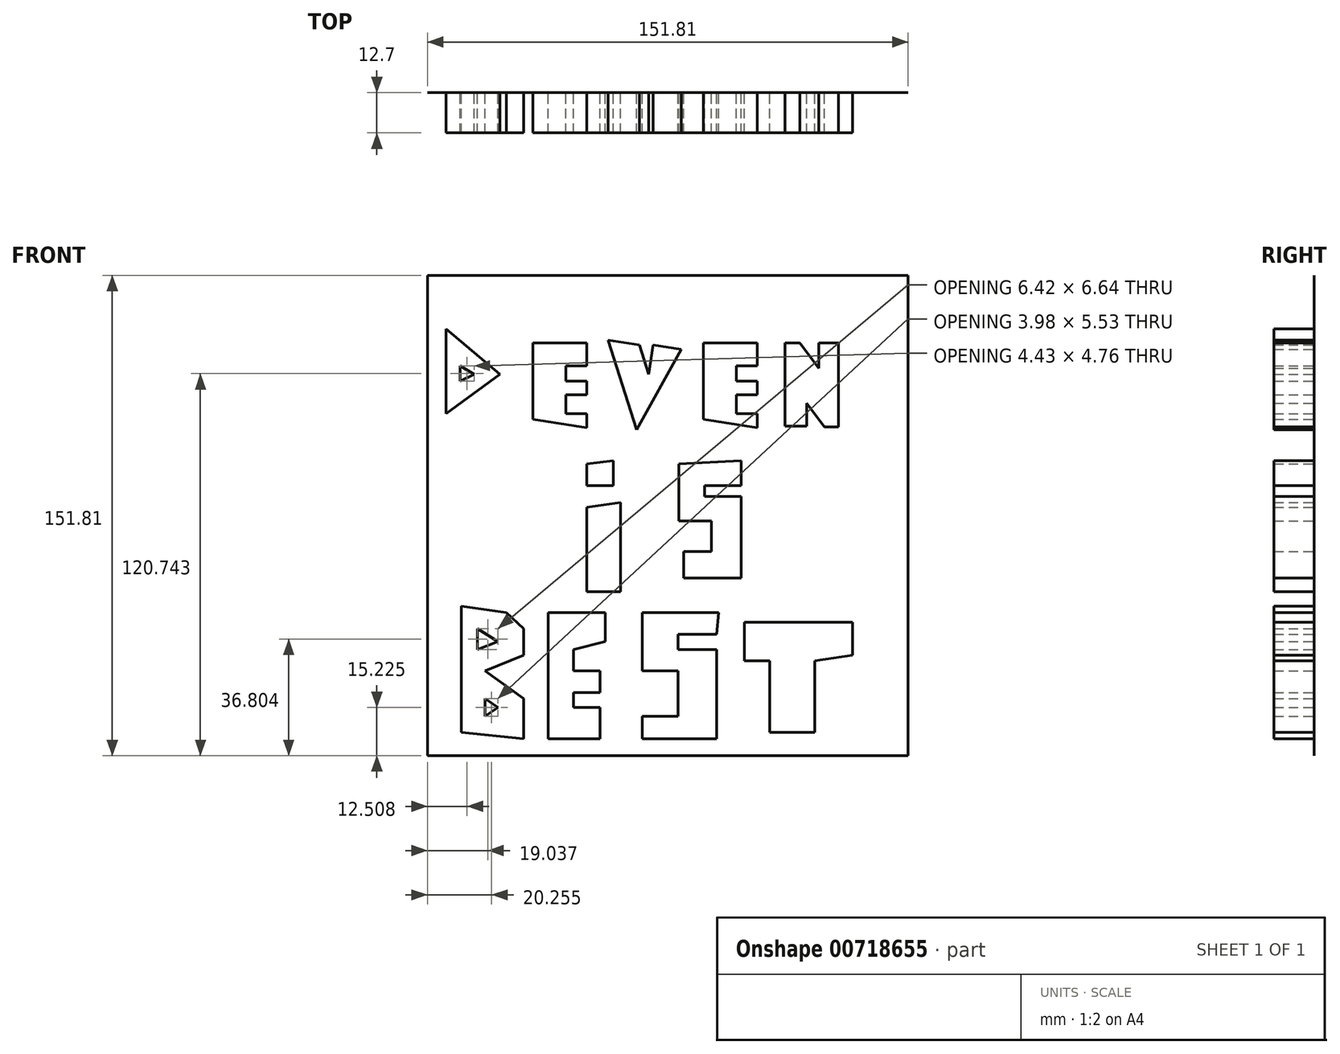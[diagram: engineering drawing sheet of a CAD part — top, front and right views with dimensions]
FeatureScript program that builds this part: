
annotation { "Feature Type Name" : "Feature", "Feature Type Description" : "" }
export const myFeature = defineFeature(function(context is Context, id is Id, definition is map)
    precondition{}
    {
        {
            var Q0;
            Q0=qCreatedBy(makeId("Front.planeOp"),FACE);
            var sketch = newSketch(context, id + "F0", { "sketchPlane" : qUnion([Q0])});
            skLineSegment(sketch, "E0", {"start": v(-70.27, 58.87) * mm, "end": v(-70.27, 32.1) * mm});
            skLineSegment(sketch, "E1", {"start": v(-70.27, 58.87) * mm, "end": v(-53.23, 44.49) * mm});
            skLineSegment(sketch, "E2", {"start": v(-70.27, 32.1) * mm, "end": v(-53.23, 44.49) * mm});
            skLineSegment(sketch, "E3", {"start": v(-42.83, 54.45) * mm, "end": v(-42.83, 30.32) * mm});
            skLineSegment(sketch, "E4", {"start": v(-65.85, 47.14) * mm, "end": v(-65.85, 42.38) * mm});
            skPoint(sketch, "E4.endSnap0", {"position": v(-42.83, 42.38) * mm});
            skLineSegment(sketch, "E5", {"start": v(-65.85, 42.38) * mm, "end": v(-61.42, 44.49) * mm});
            skLineSegment(sketch, "E6", {"start": v(-65.85, 47.14) * mm, "end": v(-61.42, 44.49) * mm});
            skLineSegment(sketch, "E7", {"start": v(-42.83, 54.45) * mm, "end": v(-25.78, 54.45) * mm});
            skLineSegment(sketch, "E8", {"start": v(-25.78, 52.68) * mm, "end": v(-25.78, 47.14) * mm});
            skLineSegment(sketch, "E9", {"start": v(-25.78, 47.14) * mm, "end": v(-32.42, 47.14) * mm});
            skLineSegment(sketch, "E10", {"start": v(-25.78, 54.45) * mm, "end": v(-25.78, 47.14) * mm});
            skLineSegment(sketch, "E11", {"start": v(-32.42, 47.14) * mm, "end": v(-32.42, 42.38) * mm});
            skLineSegment(sketch, "E12", {"start": v(-32.42, 42.38) * mm, "end": v(-25.78, 42.38) * mm});
            skLineSegment(sketch, "E13", {"start": v(-25.78, 42.38) * mm, "end": v(-25.78, 38.07) * mm});
            skLineSegment(sketch, "E14", {"start": v(-25.78, 38.07) * mm, "end": v(-32.42, 38.07) * mm});
            skLineSegment(sketch, "E15", {"start": v(-32.42, 38.07) * mm, "end": v(-32.42, 32.1) * mm});
            skLineSegment(sketch, "E16", {"start": v(-32.42, 32.1) * mm, "end": v(-25.78, 32.1) * mm});
            skLineSegment(sketch, "E17", {"start": v(-25.78, 32.1) * mm, "end": v(-25.78, 27.67) * mm});
            skLineSegment(sketch, "E18", {"start": v(-25.78, 27.67) * mm, "end": v(-42.83, 30.32) * mm});
            skLineSegment(sketch, "E19", {"start": v(-19.14, 55.33) * mm, "end": v(-10.07, 27) * mm});
            skLineSegment(sketch, "E20", {"start": v(-10.07, 27) * mm, "end": v(4.1, 52.45) * mm});
            skLineSegment(sketch, "E21", {"start": v(4.1, 52.45) * mm, "end": v(-4.8, 53.84) * mm});
            skLineSegment(sketch, "E22", {"start": v(-4.8, 53.84) * mm, "end": v(-6.24, 44.56) * mm});
            skLineSegment(sketch, "E23", {"start": v(-6.24, 44.56) * mm, "end": v(-9.22, 53.84) * mm});
            skLineSegment(sketch, "E24", {"start": v(-9.22, 53.84) * mm, "end": v(-19.14, 55.33) * mm});
            skLineSegment(sketch, "E25", {"start": v(10.97, 54.45) * mm, "end": v(10.97, 30.32) * mm});
            skPoint(sketch, "E26.endSnap0", {"position": v(10.97, 42.38) * mm});
            skLineSegment(sketch, "E27", {"start": v(10.97, 54.45) * mm, "end": v(28.01, 54.45) * mm});
            skLineSegment(sketch, "E28", {"start": v(28.01, 52.68) * mm, "end": v(28.01, 47.14) * mm});
            skLineSegment(sketch, "E29", {"start": v(28.01, 47.14) * mm, "end": v(21.37, 47.14) * mm});
            skLineSegment(sketch, "E30", {"start": v(28.01, 54.45) * mm, "end": v(28.01, 47.14) * mm});
            skLineSegment(sketch, "E31", {"start": v(21.37, 47.14) * mm, "end": v(21.37, 42.38) * mm});
            skLineSegment(sketch, "E32", {"start": v(21.37, 42.38) * mm, "end": v(28.01, 42.38) * mm});
            skLineSegment(sketch, "E33", {"start": v(28.01, 42.38) * mm, "end": v(28.01, 38.07) * mm});
            skLineSegment(sketch, "E34", {"start": v(28.01, 38.07) * mm, "end": v(21.37, 38.07) * mm});
            skLineSegment(sketch, "E35", {"start": v(21.37, 38.07) * mm, "end": v(21.37, 32.1) * mm});
            skLineSegment(sketch, "E36", {"start": v(21.37, 32.1) * mm, "end": v(28.01, 32.1) * mm});
            skLineSegment(sketch, "E37", {"start": v(28.01, 32.1) * mm, "end": v(28.01, 27.67) * mm});
            skLineSegment(sketch, "E38", {"start": v(28.01, 27.67) * mm, "end": v(10.97, 30.32) * mm});
            skLineSegment(sketch, "E39", {"start": v(36.85, 54.45) * mm, "end": v(36.85, 28.1) * mm});
            skLineSegment(sketch, "E40", {"start": v(36.85, 28.1) * mm, "end": v(43.71, 28.1) * mm});
            skLineSegment(sketch, "E41", {"start": v(43.71, 28.1) * mm, "end": v(43.71, 35.41) * mm});
            skLineSegment(sketch, "E42", {"start": v(49.25, 27.89) * mm, "end": v(53.67, 27.89) * mm});
            skLineSegment(sketch, "E43", {"start": v(53.67, 27.89) * mm, "end": v(53.67, 54.45) * mm});
            skLineSegment(sketch, "E44", {"start": v(53.67, 54.45) * mm, "end": v(47.47, 54.45) * mm});
            skLineSegment(sketch, "E45", {"start": v(47.47, 56.66) * mm, "end": v(47.47, 46.48) * mm});
            skLineSegment(sketch, "E46", {"start": v(47.47, 46.48) * mm, "end": v(41.5, 54.45) * mm});
            skLineSegment(sketch, "E47", {"start": v(41.5, 54.45) * mm, "end": v(36.85, 54.45) * mm});
            skLineSegment(sketch, "E48", {"start": v(43.71, 35.41) * mm, "end": v(49.25, 27.89) * mm});
            skSolve(sketch);
        }
        {
            var Q0;
            Q0 = qSketchRegion(id + "F0", true);
            extrude(context, id + "F1", {"entities" : qUnion([Q0]), "depth" : 12.7 * mm, "offsetDistance" : 25.4 * mm});
        }
        {
            var Q0;
            Q0=qCreatedBy(makeId("Front.planeOp"),FACE);
            var sketch = newSketch(context, id + "F2", { "sketchPlane" : qUnion([Q0])});
            skLineSegment(sketch, "E49", {"start": v(-25.78, 2.43) * mm, "end": v(-25.78, -24.13) * mm});
            skLineSegment(sketch, "E50", {"start": v(-25.78, -24.13) * mm, "end": v(-15.16, -24.13) * mm});
            skLineSegment(sketch, "E51", {"start": v(-15.16, -24.13) * mm, "end": v(-15.16, 3.98) * mm});
            skLineSegment(sketch, "E52", {"start": v(-25.78, 2.43) * mm, "end": v(-15.16, 3.98) * mm});
            skLineSegment(sketch, "E53", {"start": v(-25.78, 16.16) * mm, "end": v(-25.78, 9.3) * mm});
            skLineSegment(sketch, "E54", {"start": v(-25.78, 9.3) * mm, "end": v(-17.37, 9.3) * mm});
            skLineSegment(sketch, "E55", {"start": v(-17.37, 9.3) * mm, "end": v(-17.37, 17.26) * mm});
            skLineSegment(sketch, "E56", {"start": v(-25.78, 16.16) * mm, "end": v(-17.37, 17.26) * mm});
            skLineSegment(sketch, "E57", {"start": v(3.2, 16.16) * mm, "end": v(3.2, -1.77) * mm});
            skLineSegment(sketch, "E58", {"start": v(3.2, -1.77) * mm, "end": v(13.61, -1.77) * mm});
            skLineSegment(sketch, "E59", {"start": v(13.61, -1.77) * mm, "end": v(13.61, -11.5) * mm});
            skLineSegment(sketch, "E60", {"start": v(13.61, -11.5) * mm, "end": v(4.76, -11.5) * mm});
            skLineSegment(sketch, "E61", {"start": v(4.76, -11.5) * mm, "end": v(4.76, -19.92) * mm});
            skLineSegment(sketch, "E62", {"start": v(4.76, -19.92) * mm, "end": v(22.9, -19.92) * mm});
            skLineSegment(sketch, "E63", {"start": v(22.9, -19.92) * mm, "end": v(22.9, 5.97) * mm});
            skLineSegment(sketch, "E64", {"start": v(22.9, 5.97) * mm, "end": v(11.4, 5.97) * mm});
            skLineSegment(sketch, "E65", {"start": v(11.4, 5.97) * mm, "end": v(11.4, 9.3) * mm});
            skLineSegment(sketch, "E66", {"start": v(11.4, 9.3) * mm, "end": v(22.9, 9.3) * mm});
            skLineSegment(sketch, "E67", {"start": v(22.9, 9.3) * mm, "end": v(22.9, 17.26) * mm});
            skLineSegment(sketch, "E68", {"start": v(3.2, 16.16) * mm, "end": v(22.9, 17.26) * mm});
            skSolve(sketch);
        }
        {
            var Q0;
            Q0 = qSketchRegion(id + "F2", true);
            extrude(context, id + "F3", {"entities" : qUnion([Q0]), "depth" : 12.7 * mm, "offsetDistance" : 25.4 * mm});
        }
        {
            var Q0;
            Q0=qCreatedBy(makeId("Front.planeOp"),FACE);
            var sketch = newSketch(context, id + "F4", { "sketchPlane" : qUnion([Q0])});
            skLineSegment(sketch, "E69", {"start": v(-65.4, -28.77) * mm, "end": v(-65.4, -68.61) * mm});
            skLineSegment(sketch, "E70", {"start": v(-65.4, -28.77) * mm, "end": v(-51.24, -30.77) * mm});
            skLineSegment(sketch, "E71", {"start": v(-51.24, -30.77) * mm, "end": v(-45.7, -35.86) * mm});
            skLineSegment(sketch, "E72", {"start": v(-45.7, -35.86) * mm, "end": v(-45.7, -44.27) * mm});
            skLineSegment(sketch, "E73", {"start": v(-45.7, -44.27) * mm, "end": v(-57.88, -49.14) * mm});
            skLineSegment(sketch, "E74", {"start": v(-57.88, -49.14) * mm, "end": v(-45.7, -57.99) * mm});
            skLineSegment(sketch, "E75", {"start": v(-45.7, -57.99) * mm, "end": v(-45.7, -70.6) * mm});
            skLineSegment(sketch, "E76", {"start": v(-45.7, -70.6) * mm, "end": v(-65.4, -68.61) * mm});
            skLineSegment(sketch, "E77", {"start": v(-57.88, -57.99) * mm, "end": v(-57.88, -63.52) * mm});
            skLineSegment(sketch, "E78", {"start": v(-57.88, -57.99) * mm, "end": v(-53.9, -60.76) * mm});
            skPoint(sketch, "E78.endSnap0", {"position": v(-57.88, -60.76) * mm});
            skLineSegment(sketch, "E79", {"start": v(-57.88, -63.52) * mm, "end": v(-53.9, -60.76) * mm});
            skLineSegment(sketch, "E80", {"start": v(-60.31, -35.86) * mm, "end": v(-60.31, -42.5) * mm});
            skLineSegment(sketch, "E81", {"start": v(-60.31, -42.5) * mm, "end": v(-53.9, -39.93) * mm});
            skLineSegment(sketch, "E82", {"start": v(-53.9, -39.93) * mm, "end": v(-60.31, -35.86) * mm});
            skLineSegment(sketch, "E83", {"start": v(-37.96, -30.77) * mm, "end": v(-37.96, -70.6) * mm});
            skLineSegment(sketch, "E84", {"start": v(-37.96, -70.6) * mm, "end": v(-21.58, -70.6) * mm});
            skLineSegment(sketch, "E85", {"start": v(-21.58, -70.6) * mm, "end": v(-21.58, -60.76) * mm});
            skLineSegment(sketch, "E86", {"start": v(-21.58, -60.76) * mm, "end": v(-29.99, -60.76) * mm});
            skLineSegment(sketch, "E87", {"start": v(-29.99, -60.76) * mm, "end": v(-29.99, -56) * mm});
            skLineSegment(sketch, "E88", {"start": v(-29.99, -56) * mm, "end": v(-21.58, -56) * mm});
            skLineSegment(sketch, "E89", {"start": v(-21.58, -56) * mm, "end": v(-21.58, -49.14) * mm});
            skLineSegment(sketch, "E90", {"start": v(-21.58, -49.14) * mm, "end": v(-29.99, -49.14) * mm});
            skLineSegment(sketch, "E91", {"start": v(-29.99, -49.14) * mm, "end": v(-29.99, -42.5) * mm});
            skLineSegment(sketch, "E92", {"start": v(-37.96, -30.77) * mm, "end": v(-20.03, -30.77) * mm});
            skLineSegment(sketch, "E93", {"start": v(-20.03, -30.77) * mm, "end": v(-20.03, -39.93) * mm});
            skLineSegment(sketch, "E94", {"start": v(-29.99, -42.5) * mm, "end": v(-20.03, -39.93) * mm});
            skLineSegment(sketch, "E95", {"start": v(15.82, -30.77) * mm, "end": v(-8.3, -30.77) * mm});
            skLineSegment(sketch, "E96", {"start": v(-8.3, -30.77) * mm, "end": v(-8.3, -42.5) * mm});
            skLineSegment(sketch, "E97", {"start": v(-8.3, -42.5) * mm, "end": v(-8.3, -49.14) * mm});
            skLineSegment(sketch, "E98", {"start": v(-8.3, -49.14) * mm, "end": v(2.99, -49.14) * mm});
            skLineSegment(sketch, "E99", {"start": v(2.99, -49.14) * mm, "end": v(2.99, -63.52) * mm});
            skLineSegment(sketch, "E100", {"start": v(2.99, -63.52) * mm, "end": v(-8.3, -63.52) * mm});
            skLineSegment(sketch, "E101", {"start": v(-8.3, -63.52) * mm, "end": v(-8.3, -70.6) * mm});
            skLineSegment(sketch, "E102", {"start": v(-8.3, -70.6) * mm, "end": v(15.16, -70.6) * mm});
            skLineSegment(sketch, "E103", {"start": v(15.16, -70.6) * mm, "end": v(15.16, -42.5) * mm});
            skLineSegment(sketch, "E104", {"start": v(15.16, -42.5) * mm, "end": v(2.99, -42.5) * mm});
            skLineSegment(sketch, "E105", {"start": v(2.99, -42.5) * mm, "end": v(2.99, -37.63) * mm});
            skLineSegment(sketch, "E106", {"start": v(2.99, -37.63) * mm, "end": v(15.16, -37.63) * mm});
            skLineSegment(sketch, "E107", {"start": v(15.16, -37.63) * mm, "end": v(15.82, -30.77) * mm});
            skLineSegment(sketch, "E108", {"start": v(31.98, -52.01) * mm, "end": v(31.98, -68.61) * mm});
            skLineSegment(sketch, "E109", {"start": v(31.98, -68.61) * mm, "end": v(46.15, -68.61) * mm});
            skLineSegment(sketch, "E110", {"start": v(46.15, -68.61) * mm, "end": v(46.15, -46.04) * mm});
            skLineSegment(sketch, "E111", {"start": v(31.98, -52.01) * mm, "end": v(31.98, -46.04) * mm});
            skLineSegment(sketch, "E112", {"start": v(31.98, -46.04) * mm, "end": v(24.01, -46.04) * mm});
            skLineSegment(sketch, "E113", {"start": v(24.01, -46.04) * mm, "end": v(24.01, -33.86) * mm});
            skLineSegment(sketch, "E114", {"start": v(24.01, -33.86) * mm, "end": v(58.1, -33.86) * mm});
            skLineSegment(sketch, "E115", {"start": v(58.1, -33.86) * mm, "end": v(58.1, -44.27) * mm});
            skLineSegment(sketch, "E116", {"start": v(46.15, -46.04) * mm, "end": v(58.1, -44.27) * mm});
            skSolve(sketch);
        }
        {
            var Q0;
            Q0 = qSketchRegion(id + "F4", true);
            extrude(context, id + "F5", {"entities" : qUnion([Q0]), "depth" : 12.7 * mm, "offsetDistance" : 25.4 * mm});
        }
        {
            var Q0;
            Q0=qCreatedBy(makeId("Front.planeOp"),FACE);
            var sketch = newSketch(context, id + "F6", { "sketchPlane" : qUnion([Q0])});
            skLineSegment(sketch, "E117.bottom", {"start": v(-76.14, 75.83) * mm, "end": v(75.67, 75.83) * mm});
            skLineSegment(sketch, "E117.top", {"start": v(-76.14, -75.98) * mm, "end": v(75.67, -75.98) * mm});
            skLineSegment(sketch, "E117.left", {"start": v(-76.14, 75.83) * mm, "end": v(-76.14, -75.98) * mm});
            skLineSegment(sketch, "E117.right", {"start": v(75.67, 75.83) * mm, "end": v(75.67, -75.98) * mm});
            skSolve(sketch);
        }
        {
            var Q0;
            Q0 = qSketchRegion(id + "F6", true);
            extrude(context, id + "F7", {"entities" : qUnion([Q0]), "depth" : 0 * mm, "offsetDistance" : 25.4 * mm});
        }
    });
